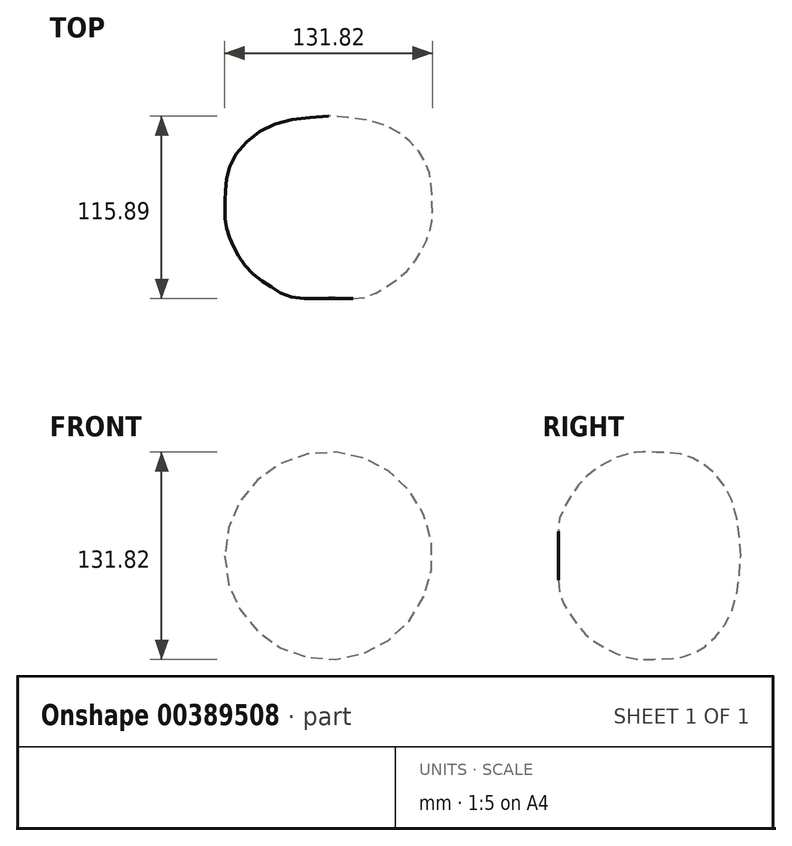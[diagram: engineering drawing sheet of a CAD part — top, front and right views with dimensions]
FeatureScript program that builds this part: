
annotation { "Feature Type Name" : "Feature", "Feature Type Description" : "" }
export const myFeature = defineFeature(function(context is Context, id is Id, definition is map)
    precondition{}
    {
        {
            var Q0;
            Q0=qCreatedBy(makeId("Top.planeOp"),FACE);
            var sketch = newSketch(context, id + "F0", { "sketchPlane" : qUnion([Q0])});
            skFitSpline(sketch, "E0", {"points": [v(0, 63.29) * mm, v(-37.03, 56.86) * mm, v(-60.07, 36.84) * mm, v(-65.36, 18.7) * mm, v(-65.74, 6.99) * mm, v(-65.74, -2.83) * mm, v(-63.1, -13.41) * mm, v(-57.8, -24.37) * mm, v(-48.36, -36.84) * mm, v(-36.27, -45.53) * mm, v(-23.05, -51.95) * mm, v(0, -51.95) * mm], "startDerivative": vector(-291.13, -17.51) * mm, "endDerivative": vector(238.86, 5.37) * mm});
            skLineSegment(sketch, "E1", {"start": v(0, 63.29) * mm, "end": v(0, -51.95) * mm});
            skSolve(sketch);
        }
        {
            var Q0;
            Q0=makeQuery(id+"F0.imprint","IMPRINT",FACE,{"disambiguationData":[TD([[makeQuery(id+"F0.imprint","IMPRINT",EDGE,{"derivedFrom":sQuery(id+"F0.wireOp",EDGE,"E0")}),1.0]])]});
            var Q1;
            Q1=sQuery(id+"F0.wireOp",EDGE,"E1");
            revolve(context, id + "F1", {"entities" : qUnion([Q0]), "axis" : qUnion([Q1]), "revolveType" : RevolveType.FULL});
        }
    });
